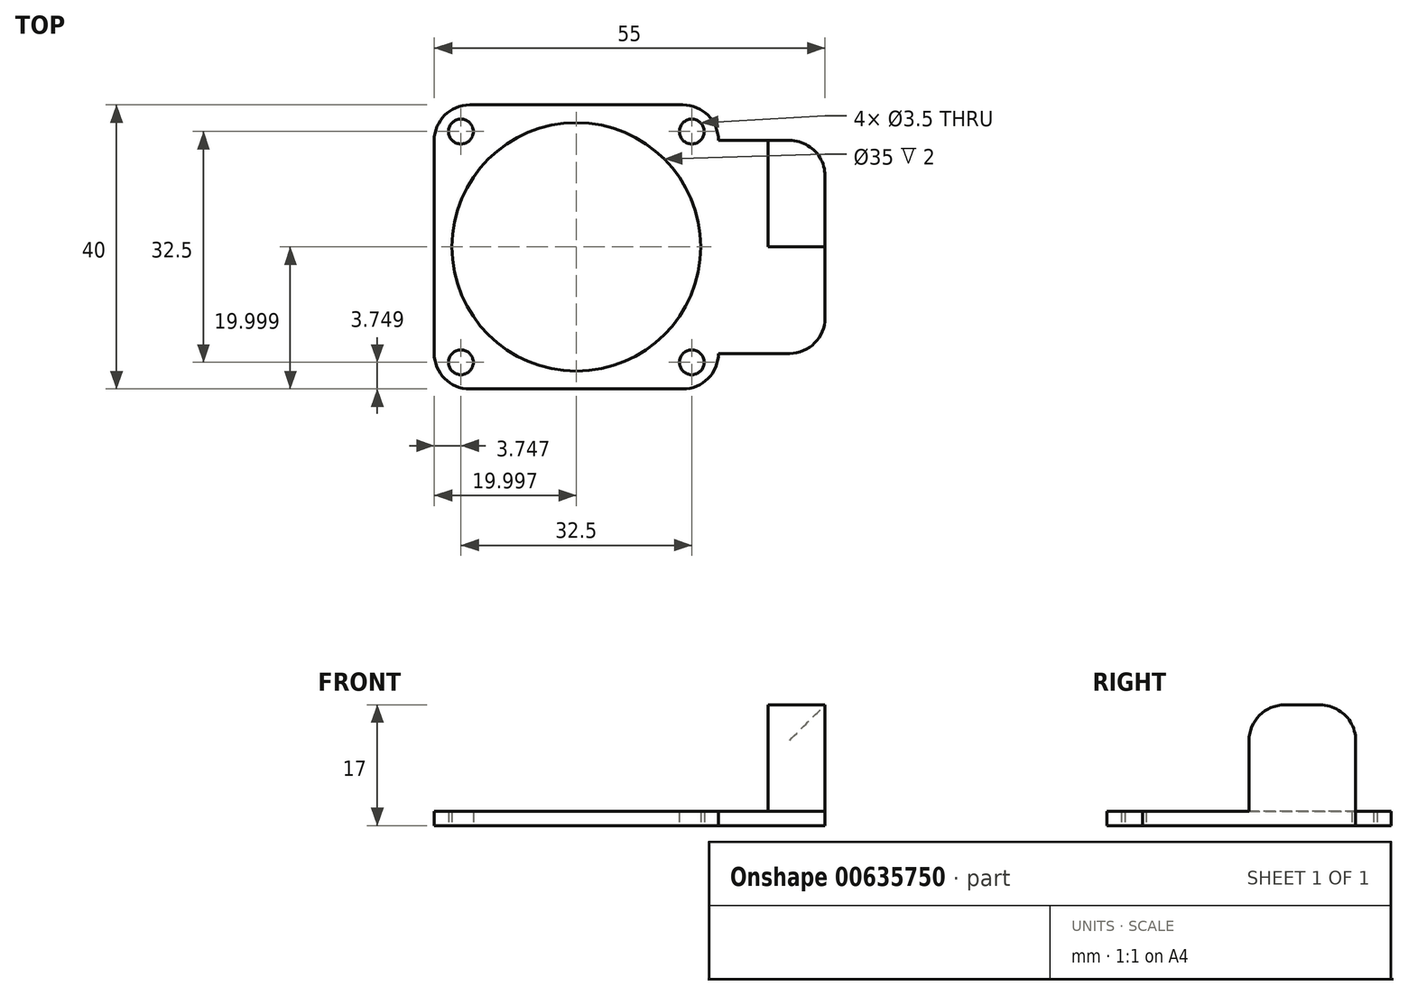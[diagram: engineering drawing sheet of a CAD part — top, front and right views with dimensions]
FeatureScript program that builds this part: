
annotation { "Feature Type Name" : "Feature", "Feature Type Description" : "" }
export const myFeature = defineFeature(function(context is Context, id is Id, definition is map)
    precondition{}
    {
        {
            var Q0;
            Q0=qCreatedBy(makeId("Top.planeOp"),FACE);
            var sketch = newSketch(context, id + "F0", { "sketchPlane" : qUnion([Q0])});
            skLineSegment(sketch, "E0.bottom", {"start": v(29.02, -46.04) * mm, "end": v(-10.98, -46.04) * mm});
            skLineSegment(sketch, "E0.top", {"start": v(29.02, -6.04) * mm, "end": v(-10.98, -6.04) * mm});
            skLineSegment(sketch, "E0.left", {"start": v(29.02, -46.04) * mm, "end": v(29.02, -6.04) * mm});
            skLineSegment(sketch, "E0.right", {"start": v(-10.98, -46.04) * mm, "end": v(-10.98, -6.04) * mm});
            skPoint(sketch, "E0.middle", {"position": v(9.02, -26.04) * mm});
            skCircle(sketch, "E1", {"center": v(-7.23, -9.8) * mm, "radius": 1.75 * mm});
            skCircle(sketch, "E2", {"center": v(25.27, -9.8) * mm, "radius": 1.75 * mm});
            skCircle(sketch, "E3", {"center": v(25.27, -42.3) * mm, "radius": 1.75 * mm});
            skCircle(sketch, "E4", {"center": v(-7.23, -42.3) * mm, "radius": 1.75 * mm});
            skCircle(sketch, "E5", {"center": v(9.02, -26.04) * mm, "radius": 17.5 * mm});
            skSolve(sketch);
        }
        {
            var Q0;
            Q0 = qSketchRegion(id + "F0", true);
            extrude(context, id + "F1", {"entities" : qUnion([Q0]), "depth" : 2 * mm, "offsetDistance" : 25 * mm});
        }
        {
            var Q0;
            Q0=makeQuery(id+"F1.opExtrude","SWEPT_EDGE",EDGE,{"disambiguationData":[OSD([sQuery(id+"F0.wireOp",EDGE,"E0.bottom"),sQuery(id+"F0.wireOp",EDGE,"E0.left")])]});
            var Q1;
            Q1=makeQuery(id+"F1.opExtrude","SWEPT_EDGE",EDGE,{"disambiguationData":[OSD([sQuery(id+"F0.wireOp",EDGE,"E0.top"),sQuery(id+"F0.wireOp",EDGE,"E0.left")])]});
            var Q2;
            Q2=makeQuery(id+"F1.opExtrude","SWEPT_EDGE",EDGE,{"disambiguationData":[OSD([sQuery(id+"F0.wireOp",EDGE,"E0.bottom"),sQuery(id+"F0.wireOp",EDGE,"E0.right")])]});
            var Q3;
            Q3=makeQuery(id+"F1.opExtrude","SWEPT_EDGE",EDGE,{"disambiguationData":[OSD([sQuery(id+"F0.wireOp",EDGE,"E0.top"),sQuery(id+"F0.wireOp",EDGE,"E0.right")])]});
            fillet(context, id + "F2", {"entities" : qUnion([Q0, Q1, Q2, Q3]), "radius" : 5 * mm, "tangentPropagation" : true, "allowEdgeOverflow" : false});
        }
        {
            var Q0;
            Q0=makeQuery(id+"F1.opExtrude","SWEPT_FACE",FACE,{"disambiguationData":[OSD([sQuery(id+"F0.wireOp",EDGE,"E0.left")])]});
            extrude(context, id + "F3", {"entities" : qUnion([Q0]), "operationType" : NewBodyOperationType.ADD, "depth" : 15 * mm, "offsetDistance" : 25 * mm});
        }
        {
            var Q0;
            {var subQ0=sQuery(id+"F0.wireOp",EDGE,"E0.left");Q0=makeQuery(id+"F3.boolean.opBoolean","MERGE",FACE,{"derivedFrom":[makeQuery(id+"F1.opExtrude","CAP_FACE",FACE,{"disambiguationData":[OSD([sQuery(id+"F0.wireOp",EDGE,"E0.bottom"),sQuery(id+"F0.wireOp",EDGE,"E0.top"),subQ0,sQuery(id+"F0.wireOp",EDGE,"E0.right"),sQuery(id+"F0.wireOp",EDGE,"E1"),sQuery(id+"F0.wireOp",EDGE,"E2"),sQuery(id+"F0.wireOp",EDGE,"E3"),sQuery(id+"F0.wireOp",EDGE,"E4"),sQuery(id+"F0.wireOp",EDGE,"E5")])],"isStart":false}),makeQuery(id+"F3.opExtrude","SWEPT_FACE",FACE,{"disambiguationData":[OSD([subQ0]),TDD([makeQuery(id+"F1.opExtrude","CAP_EDGE",EDGE,{"disambiguationData":[OSD([subQ0])],"isStart":false})])]})]});}
            var sketch = newSketch(context, id + "F4", { "sketchPlane" : qUnion([Q0])});
            skLineSegment(sketch, "E6.bottom", {"start": v(44.02, -11.04) * mm, "end": v(36.02, -11.04) * mm});
            skLineSegment(sketch, "E6.top", {"start": v(44.02, -26.04) * mm, "end": v(36.02, -26.04) * mm});
            skLineSegment(sketch, "E6.left", {"start": v(44.02, -11.04) * mm, "end": v(44.02, -26.04) * mm});
            skLineSegment(sketch, "E6.right", {"start": v(36.02, -11.04) * mm, "end": v(36.02, -26.04) * mm});
            skSolve(sketch);
        }
        {
            var Q0;
            Q0 = qSketchRegion(id + "F4", true);
            extrude(context, id + "F5", {"entities" : qUnion([Q0]), "operationType" : NewBodyOperationType.ADD, "depth" : 15 * mm, "offsetDistance" : 25 * mm});
        }
        {
            var Q0;
            Q0=makeQuery(id+"F3.opExtrude","CAP_EDGE",EDGE,{"disambiguationData":[OSD([sQuery(id+"F0.wireOp",EDGE,"E0.bottom"),sQuery(id+"F0.wireOp",EDGE,"E0.left")])],"isStart":false});
            var Q1;
            Q1=makeQuery(id+"F5.opExtrude","CAP_EDGE",EDGE,{"disambiguationData":[OSD([sQuery(id+"F4.wireOp",EDGE,"E6.top")])],"isStart":false});
            var Q2;
            Q2=makeQuery(id+"F5.opExtrude","CAP_EDGE",EDGE,{"disambiguationData":[OSD([sQuery(id+"F4.wireOp",EDGE,"E6.bottom")])],"isStart":false});
            var Q3;
            Q3=makeQuery(id+"F5.boolean.opBoolean","MERGE",EDGE,{"derivedFrom":[makeQuery(id+"F3.opExtrude","CAP_EDGE",EDGE,{"disambiguationData":[OSD([sQuery(id+"F0.wireOp",EDGE,"E0.top"),sQuery(id+"F0.wireOp",EDGE,"E0.left")])],"isStart":false}),makeQuery(id+"F5.opExtrude","SWEPT_EDGE",EDGE,{"disambiguationData":[OSD([sQuery(id+"F4.wireOp",EDGE,"E6.bottom"),sQuery(id+"F4.wireOp",EDGE,"E6.left")])]})]});
            fillet(context, id + "F6", {"entities" : qUnion([Q0, Q1, Q2, Q3]), "radius" : 5 * mm, "tangentPropagation" : true, "allowEdgeOverflow" : false});
        }
    });
